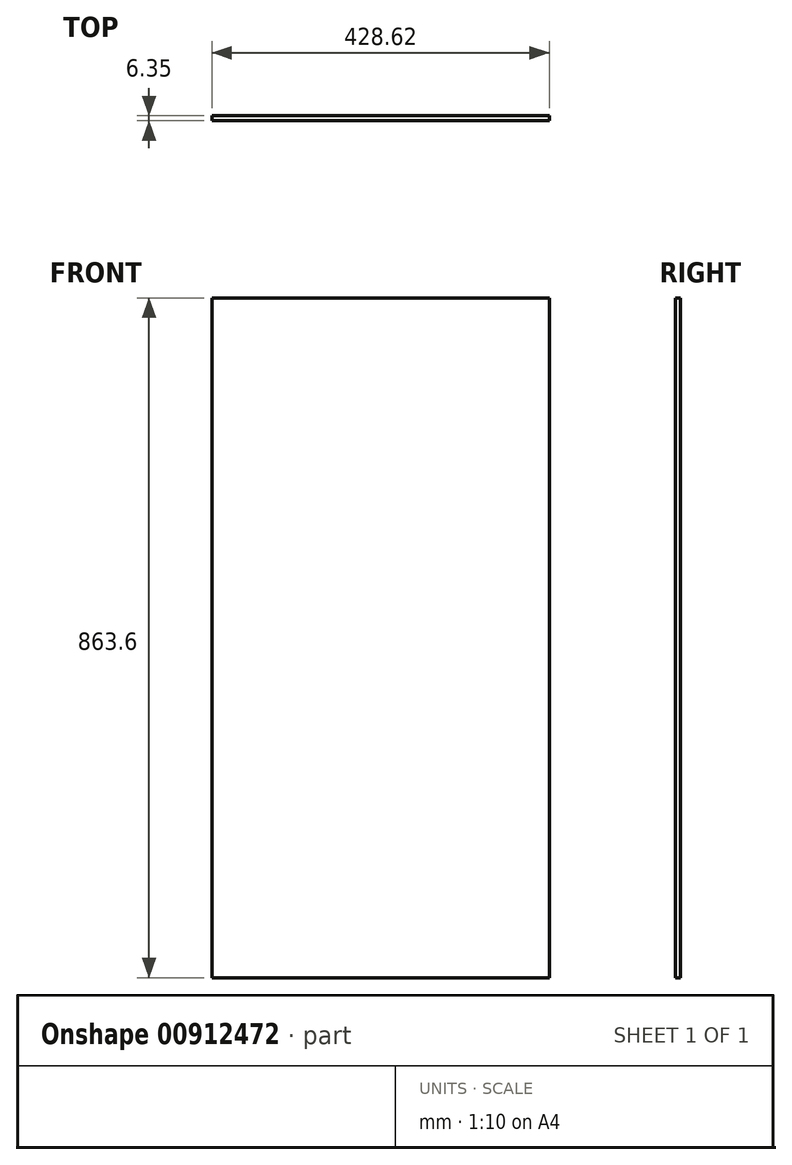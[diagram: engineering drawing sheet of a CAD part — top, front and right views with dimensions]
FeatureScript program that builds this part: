
annotation { "Feature Type Name" : "Feature", "Feature Type Description" : "" }
export const myFeature = defineFeature(function(context is Context, id is Id, definition is map)
    precondition{}
    {
        {
            var Q0;
            Q0=qCreatedBy(makeId("Front.planeOp"),FACE);
            var sketch = newSketch(context, id + "F0", { "sketchPlane" : qUnion([Q0])});
            skLineSegment(sketch, "E0.bottom", {"start": v(0, 0) * mm, "end": v(428.62, 0) * mm});
            skLineSegment(sketch, "E0.top", {"start": v(0, 863.6) * mm, "end": v(428.62, 863.6) * mm});
            skLineSegment(sketch, "E0.left", {"start": v(0, 0) * mm, "end": v(0, 863.6) * mm});
            skLineSegment(sketch, "E0.right", {"start": v(428.62, 0) * mm, "end": v(428.62, 863.6) * mm});
            skSolve(sketch);
        }
        {
            var Q0;
            Q0 = qSketchRegion(id + "F0", true);
            extrude(context, id + "F1", {"entities" : qUnion([Q0]), "depth" : 6.35 * mm, "offsetDistance" : 25.4 * mm});
        }
    });
